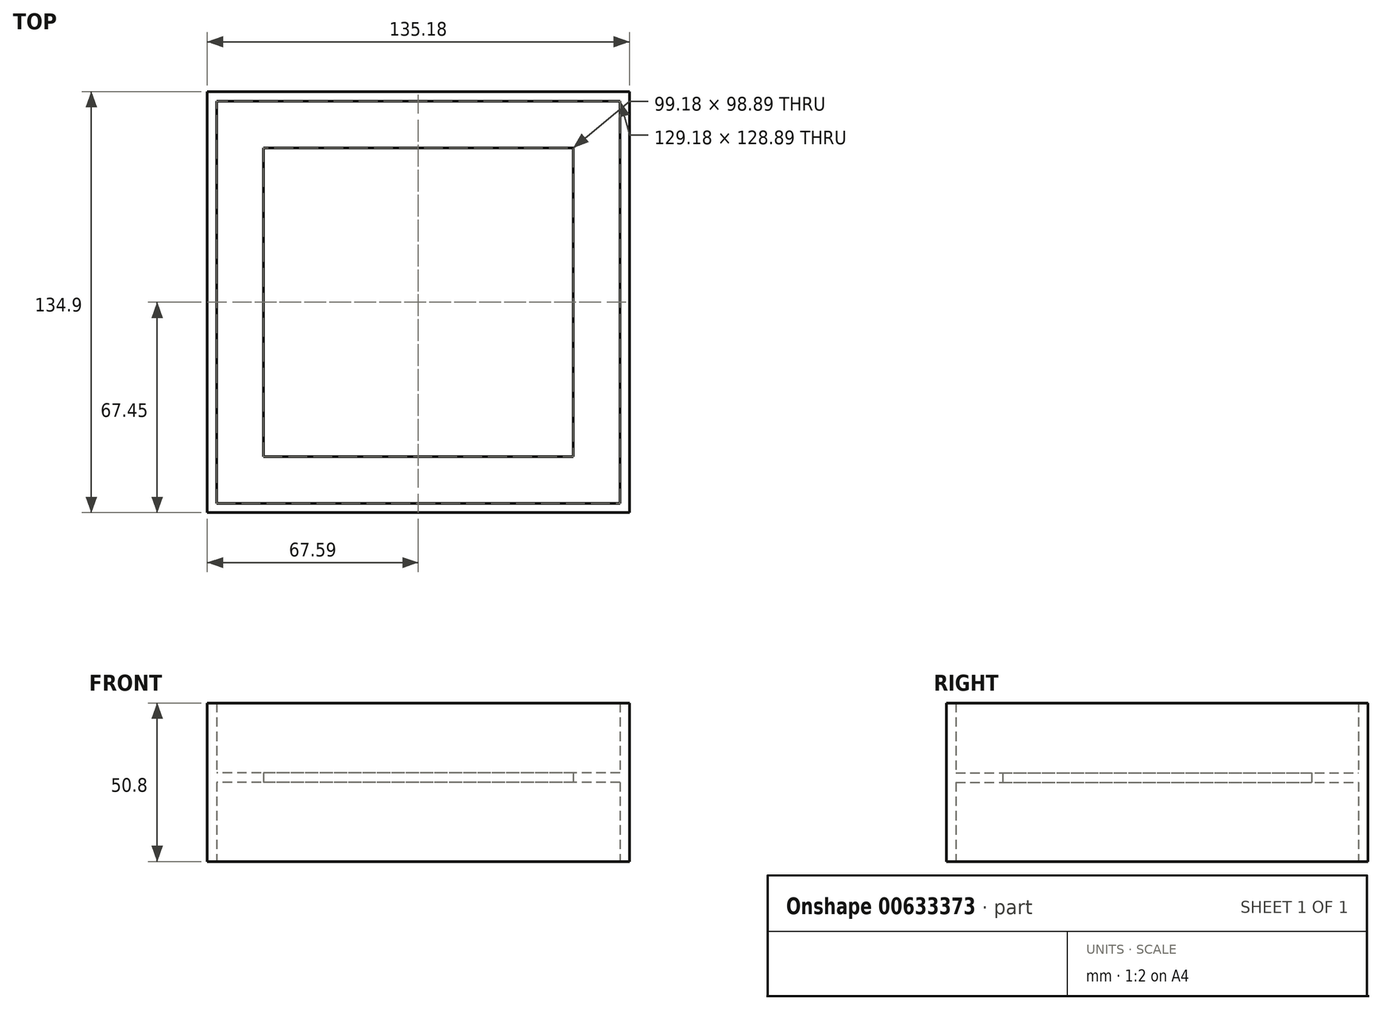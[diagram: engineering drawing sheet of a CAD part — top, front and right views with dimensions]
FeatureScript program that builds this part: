
annotation { "Feature Type Name" : "Feature", "Feature Type Description" : "" }
export const myFeature = defineFeature(function(context is Context, id is Id, definition is map)
    precondition{}
    {
        {
            var Q0;
            Q0=qCreatedBy(makeId("Top.planeOp"),FACE);
            var sketch = newSketch(context, id + "F0", { "sketchPlane" : qUnion([Q0])});
            skLineSegment(sketch, "E0.bottom", {"start": v(64.6, -64.45) * mm, "end": v(-64.6, -64.45) * mm});
            skLineSegment(sketch, "E0.top", {"start": v(64.6, 64.45) * mm, "end": v(-64.6, 64.45) * mm});
            skLineSegment(sketch, "E0.left", {"start": v(64.6, -64.45) * mm, "end": v(64.6, 64.45) * mm});
            skLineSegment(sketch, "E0.right", {"start": v(-64.6, -64.45) * mm, "end": v(-64.6, 64.45) * mm});
            skPoint(sketch, "E0.middle", {"position": v(0, 0) * mm});
            skLineSegment(sketch, "E1.bottom", {"start": v(49.6, -49.45) * mm, "end": v(-49.6, -49.45) * mm});
            skLineSegment(sketch, "E1.top", {"start": v(49.6, 49.45) * mm, "end": v(-49.6, 49.45) * mm});
            skLineSegment(sketch, "E1.left", {"start": v(49.6, -49.45) * mm, "end": v(49.6, 49.45) * mm});
            skLineSegment(sketch, "E1.right", {"start": v(-49.6, -49.45) * mm, "end": v(-49.6, 49.45) * mm});
            skSolve(sketch);
        }
        {
            var Q0;
            Q0=makeQuery(id+"F0.imprint","IMPRINT",FACE,{"disambiguationData":[TD([[makeQuery(id+"F0.imprint","IMPRINT",EDGE,{"derivedFrom":sQuery(id+"F0.wireOp",EDGE,"E0.bottom")}),-1.0]])]});
            extrude(context, id + "F1", {"entities" : qUnion([Q0]), "depth" : 3 * mm, "offsetDistance" : 25.4 * mm});
        }
        {
            var Q0;
            Q0=qCreatedBy(makeId("Top.planeOp"),FACE);
            var sketch = newSketch(context, id + "F2", { "sketchPlane" : qUnion([Q0])});
            skLineSegment(sketch, "E2.bottom", {"start": v(67.6, -67.45) * mm, "end": v(-67.6, -67.45) * mm});
            skLineSegment(sketch, "E2.top", {"start": v(67.6, 67.45) * mm, "end": v(-67.6, 67.45) * mm});
            skLineSegment(sketch, "E2.left", {"start": v(67.6, -67.45) * mm, "end": v(67.6, 67.45) * mm});
            skLineSegment(sketch, "E2.right", {"start": v(-67.6, -67.45) * mm, "end": v(-67.6, 67.45) * mm});
            skPoint(sketch, "E2.middle", {"position": v(0, 0) * mm});
            skLineSegment(sketch, "E3.bottom", {"start": v(64.6, -64.45) * mm, "end": v(-64.6, -64.45) * mm});
            skLineSegment(sketch, "E3.top", {"start": v(64.6, 64.45) * mm, "end": v(-64.6, 64.45) * mm});
            skLineSegment(sketch, "E3.left", {"start": v(64.6, -64.45) * mm, "end": v(64.6, 64.45) * mm});
            skLineSegment(sketch, "E3.right", {"start": v(-64.6, -64.45) * mm, "end": v(-64.6, 64.45) * mm});
            skSolve(sketch);
        }
        {
            var Q0;
            Q0=makeQuery(id+"F2.imprint","IMPRINT",FACE,{"disambiguationData":[TD([[makeQuery(id+"F2.imprint","IMPRINT",EDGE,{"derivedFrom":sQuery(id+"F2.wireOp",EDGE,"E2.bottom")}),-1.0]])]});
            extrude(context, id + "F3", {"entities" : qUnion([Q0]), "operationType" : NewBodyOperationType.ADD, "depth" : 25.4 * mm, "offsetDistance" : 25.4 * mm, "hasSecondDirection" : true, "secondDirectionOppositeDirection" : true, "secondDirectionDepth" : 25.4 * mm});
        }
    });
